# Revit family: ABR7015PB
name_source: partatom
category: Detail Items
revit_build: Autodesk Revit 2016 (Build: 20150220_1215(x64)
units: mm (PartAtom-declared; Revit-internal decimal feet)

## family parameters
OmniClass Number = 23.20.40.11.24.14
OmniClass Title = Wood Connectors
Rotate with component = No
Shared = No

## types (4) — shared parameters
Density = 0.08 kg
Description = Angle brackets
EPD = https://www.strongtie.eu
ETA / DoP = https://www.strongtie.eu
Manufacturer = Simpson Strong-Tie
Model = ABR7015PB
Model Disclaimer = Contact Simpson Strong-Tie Company  for more information
Model ID = 0175791697968029275530011542125471212646
Name = ABR7015PB
ObjectType = ABR7015PB
Product Material = Zpro® + black painting
Product Type = Angle brackets
Reference = ABR7015PB
Technical datasheet = https://www.strongtie.eu
URL = www.strongtie.eu
UniClass Number = Pr_20_85_09_09
UniClass Title = Bracketed angle supports

## per-type parameters (varying)
| type | _visiblefront | _visibleleft | _visibleright | _visibletop |
| SST_ABR7015PB_Front | Yes | No | No | No |
| SST_ABR7015PB_Top | No | No | No | Yes |
| SST_ABR7015PB_Left | No | Yes | No | No |
| SST_ABR7015PB_Right | No | No | Yes | No |
